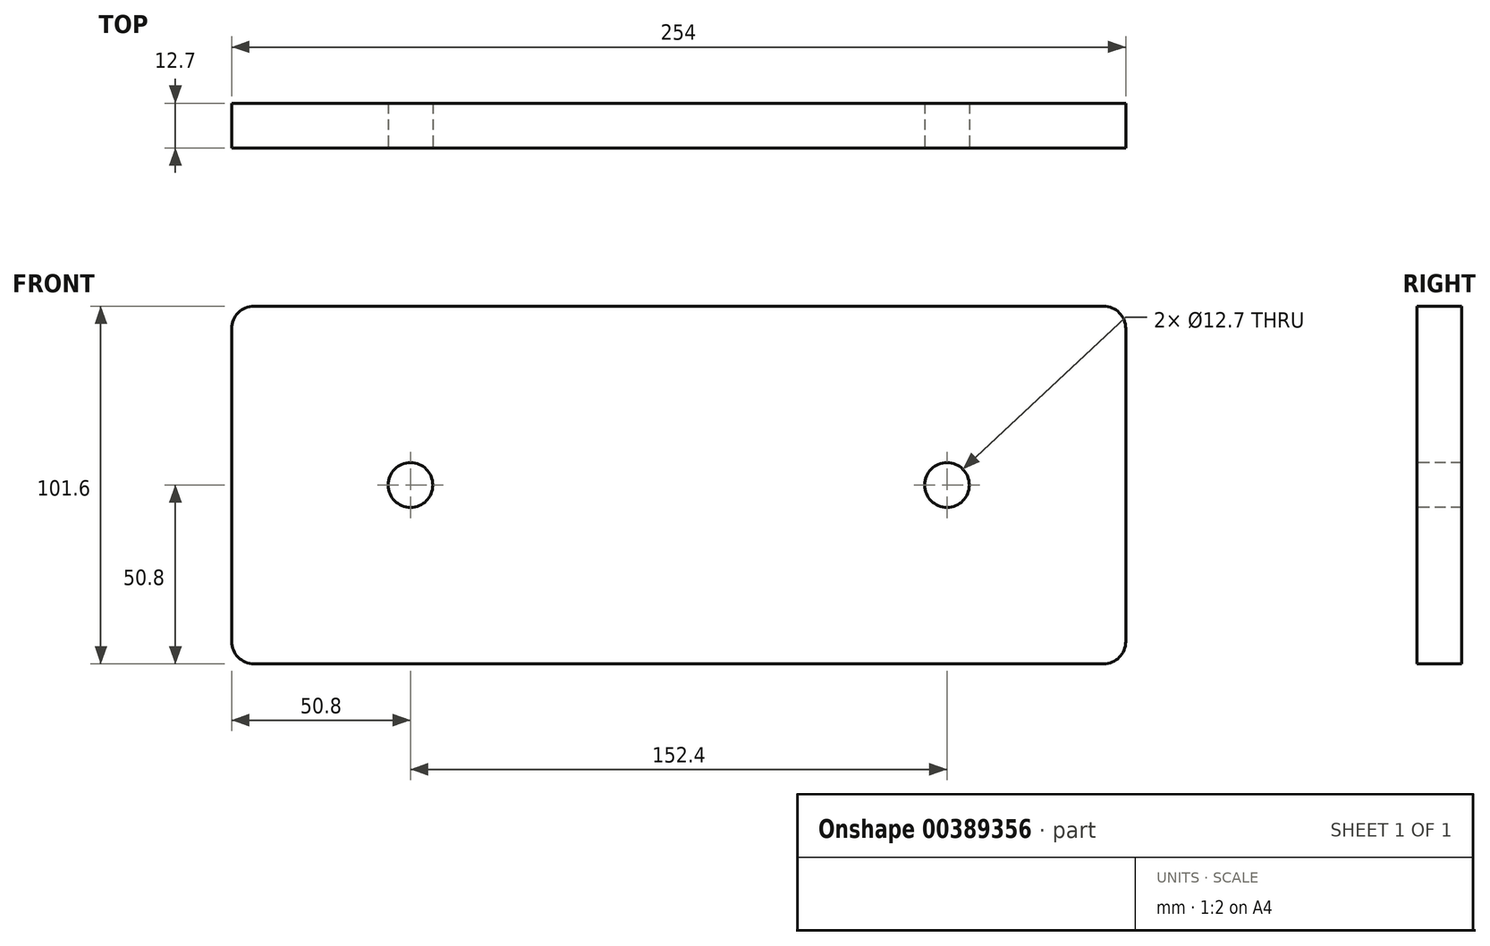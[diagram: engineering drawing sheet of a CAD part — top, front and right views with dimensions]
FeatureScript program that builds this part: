
annotation { "Feature Type Name" : "Feature", "Feature Type Description" : "" }
export const myFeature = defineFeature(function(context is Context, id is Id, definition is map)
    precondition{}
    {
        {
            var Q0;
            Q0=qCreatedBy(makeId("Front.planeOp"),FACE);
            var sketch = newSketch(context, id + "F0", { "sketchPlane" : qUnion([Q0])});
            skLineSegment(sketch, "E0.bottom", {"start": v(0, 0) * mm, "end": v(254, 0) * mm});
            skLineSegment(sketch, "E0.top", {"start": v(0, 101.6) * mm, "end": v(254, 101.6) * mm});
            skLineSegment(sketch, "E0.left", {"start": v(0, 0) * mm, "end": v(0, 101.6) * mm});
            skLineSegment(sketch, "E0.right", {"start": v(254, 0) * mm, "end": v(254, 101.6) * mm});
            skSolve(sketch);
        }
        {
            var Q0;
            Q0 = qSketchRegion(id + "F0", true);
            extrude(context, id + "F1", {"entities" : qUnion([Q0]), "depth" : 12.7 * mm});
        }
        {
            var Q0;
            Q0=makeQuery(id+"F1.opExtrude","CAP_FACE",FACE,{"disambiguationData":[OSD([sQuery(id+"F0.wireOp",EDGE,"E0.bottom"),sQuery(id+"F0.wireOp",EDGE,"E0.top"),sQuery(id+"F0.wireOp",EDGE,"E0.left"),sQuery(id+"F0.wireOp",EDGE,"E0.right")])],"isStart":false});
            var sketch = newSketch(context, id + "F2", { "sketchPlane" : qUnion([Q0])});
            skCircle(sketch, "E1", {"center": v(50.8, 50.8) * mm, "radius": 6.35 * mm});
            skPoint(sketch, "E1.centerSnap0", {"position": v(0, 50.8) * mm});
            skCircle(sketch, "E2", {"center": v(203.2, 50.8) * mm, "radius": 6.35 * mm});
            skSolve(sketch);
        }
        {
            var Q0;
            Q0=makeQuery(id+"F2.imprint","IMPRINT",FACE,{"disambiguationData":[TD([[makeQuery(id+"F2.imprint","IMPRINT",EDGE,{"derivedFrom":sQuery(id+"F2.wireOp",EDGE,"E1")}),1.0]])]});
            var Q1;
            Q1=makeQuery(id+"F2.imprint","IMPRINT",FACE,{"disambiguationData":[TD([[makeQuery(id+"F2.imprint","IMPRINT",EDGE,{"derivedFrom":sQuery(id+"F2.wireOp",EDGE,"E2")}),1.0]])]});
            extrude(context, id + "F3", {"entities" : qUnion([Q0, Q1]), "operationType" : NewBodyOperationType.REMOVE, "oppositeDirection" : true, "depth" : 12.7 * mm});
        }
        {
            var Q0;
            Q0=makeQuery(id+"F1.opExtrude","SWEPT_EDGE",EDGE,{"disambiguationData":[OSD([sQuery(id+"F0.wireOp",EDGE,"E0.top"),sQuery(id+"F0.wireOp",EDGE,"E0.left")])]});
            var Q1;
            Q1=makeQuery(id+"F1.opExtrude","SWEPT_EDGE",EDGE,{"disambiguationData":[OSD([sQuery(id+"F0.wireOp",EDGE,"E0.bottom"),sQuery(id+"F0.wireOp",EDGE,"E0.right")])]});
            var Q2;
            Q2=makeQuery(id+"F1.opExtrude","SWEPT_EDGE",EDGE,{"disambiguationData":[OSD([sQuery(id+"F0.wireOp",EDGE,"E0.top"),sQuery(id+"F0.wireOp",EDGE,"E0.right")])]});
            var Q3;
            Q3=makeQuery(id+"F1.opExtrude","SWEPT_EDGE",EDGE,{"disambiguationData":[OSD([sQuery(id+"F0.wireOp",EDGE,"E0.bottom"),sQuery(id+"F0.wireOp",EDGE,"E0.left")])]});
            fillet(context, id + "F4", {"entities" : qUnion([Q0, Q1, Q2, Q3]), "radius" : 6.35 * mm, "tangentPropagation" : true, "allowEdgeOverflow" : false});
        }
    });
